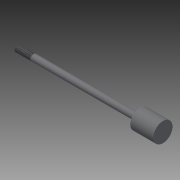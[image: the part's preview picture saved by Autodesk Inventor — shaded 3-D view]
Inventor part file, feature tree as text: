
AUTODESK INVENTOR PART (.ipt)
format: ipt  version: 2014 (Build 180170000, 170)  size: 125,440 bytes
history: native  units: in
note: dims shown in document units (in); Inventor stores cm internally (conversion verified against a paired STEP export)
features: other x49, revolve x3, sketch x3, thread x1
ambient origin geometry x8: Origin, YZ Plane, XZ Plane, XY Plane, X Axis, Y Axis, Z Axis, Center Point
bodies: Solid1 (feature_tree)
feature tree (56):
  revolve  "Revolution1"  [1 undecoded]
  thread  "Thread1"  [1 undecoded]
  revolve  "Revolution2"  [1 undecoded]
  revolve  "Revolution3"  [1 undecoded]
  other  "h1_XY"
  other  "h1_YZ"
  other  "h1_ZX"
  other  "h1_X"
  other  "h1_Y"
  other  "h1_Z"
  other  "h1_Center"
  other  "h2_XY"
  other  "h2_YZ"
  other  "h2_ZX"
  other  "h2_X"
  other  "h2_Y"
  other  "h2_Z"
  other  "h2_Center"
  other  "k1_XY"
  other  "k1_YZ"
  other  "k1_ZX"
  other  "k1_X"
  other  "k1_Y"
  other  "k1_Z"
  other  "k1_Center"
  other  "k2_XY"
  other  "k2_YZ"
  other  "k2_ZX"
  other  "k2_X"
  other  "k2_Y"
  other  "k2_Z"
  other  "k2_Center"
  other  "start_XY"
  other  "start_YZ"
  other  "start_ZX"
  other  "start_X"
  other  "start_Y"
  other  "start_Z"
  other  "start_Center"
  other  "to_prc_XY"
  other  "to_prc_YZ"
  other  "to_prc_ZX"
  other  "to_prc_X"
  other  "to_prc_Y"
  other  "to_prc_Z"
  other  "to_prc_Center"
  other  "to_rod_guide_XY"
  other  "to_rod_guide_YZ"
  other  "to_rod_guide_ZX"
  other  "to_rod_guide_X"
  other  "to_rod_guide_Y"
  other  "to_rod_guide_Z"
  other  "to_rod_guide_Center"
  sketch  "Sketch_3"  dims[d0=360.0deg d1=0.49in d2=3.791in d3=360.0deg]
  sketch  "Sketch_17"
  sketch  "Sketch_12"  dims[d4=360.0deg]
note: 4 required parameter values undecoded (feature->parameter linkage not recoverable at this tier; creation-order binding heuristic only, values carry confidence <= 0.55)